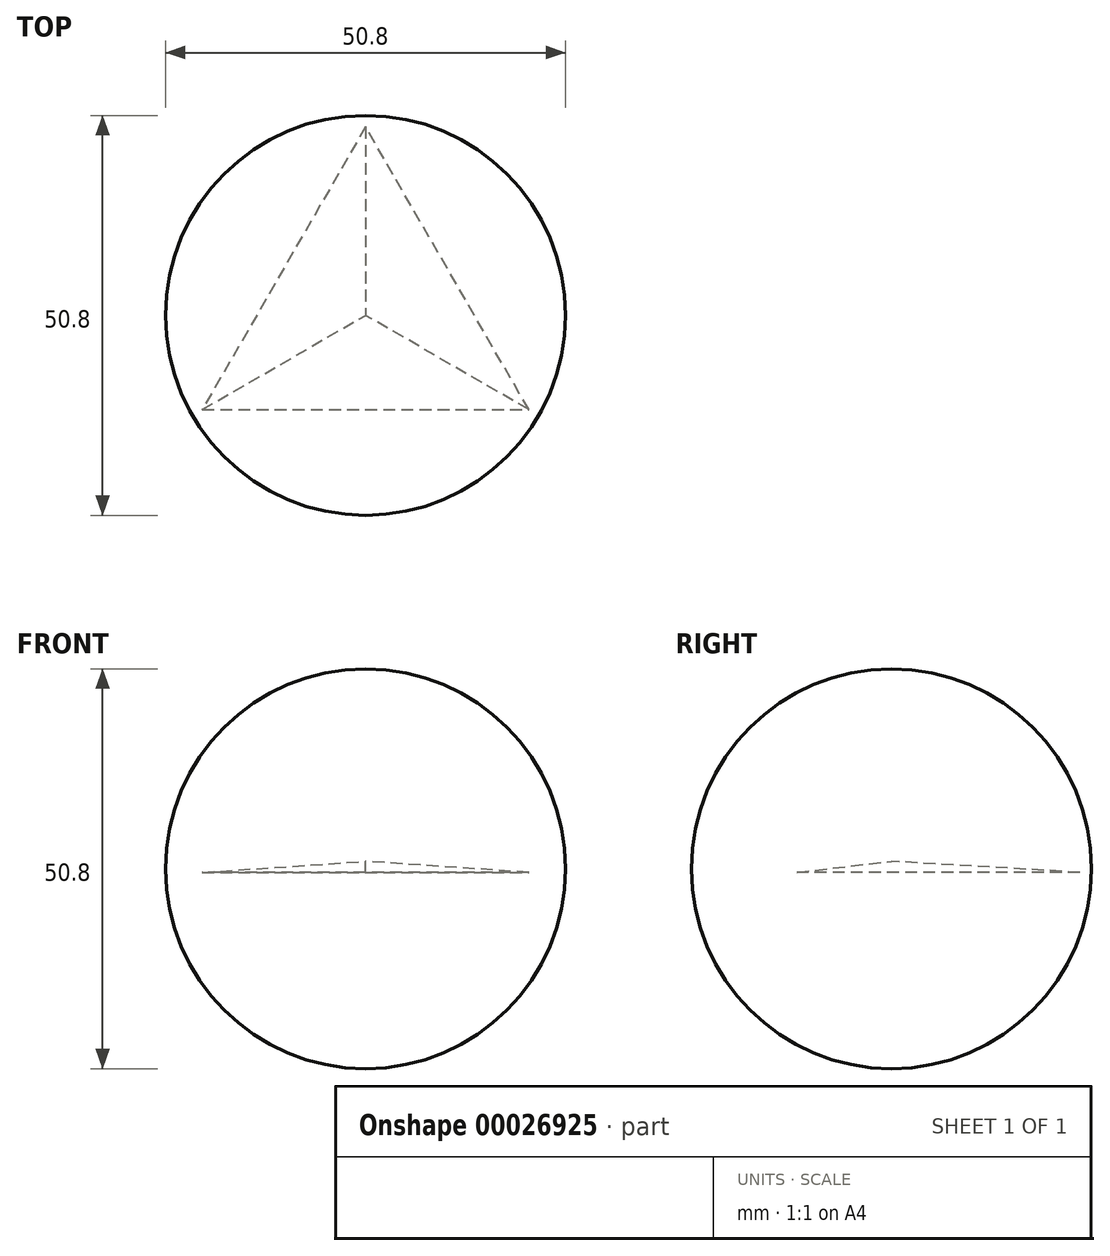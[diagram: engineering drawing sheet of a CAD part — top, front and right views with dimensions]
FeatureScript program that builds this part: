
annotation { "Feature Type Name" : "Feature", "Feature Type Description" : "" }
export const myFeature = defineFeature(function(context is Context, id is Id, definition is map)
    precondition{}
    {
        {
            assignVariable(context, id + "F0", {"name" : "r", "anyValue" : 1});
        }
        {
            assignVariable(context, id + "F1", {"name" : "s", "anyValue" : sqrt(8 / 3) * getVariable(context, 'r')});
        }
        {
            assignVariable(context, id + "F2", {"name" : "h", "anyValue" : sqrt((getVariable(context, 's')) ^ 2 - (getVariable(context, 's') / 2) ^ 2)});
        }
        {
            var Q0;
            Q0=qCreatedBy(makeId("Top.planeOp"),FACE);
            var sketch = newSketch(context, id + "F3", { "sketchPlane" : qUnion([Q0])});
            skLineSegment(sketch, "E0", {"start": v(0, 0) * mm, "end": v(0, 25.4) * mm});
            skLineSegment(sketch, "E1", {"start": v(0, 0) * mm, "end": v(25.4, 0) * mm});
            skArc(sketch, "E2", {"start": v(25.4, 0) * mm, "mid": v(17.96, 17.96) * mm, "end": v(0, 25.4) * mm});
            skSolve(sketch);
        }
        {
            var Q0;
            Q0=makeQuery(id+"F3.imprint","IMPRINT",FACE,{"disambiguationData":[TD([[makeQuery(id+"F3.imprint","IMPRINT",EDGE,{"derivedFrom":sQuery(id+"F3.wireOp",EDGE,"E0")}),-1.0]])]});
            var Q1;
            Q1=sQuery(id+"F3.wireOp",EDGE,"E0");
            revolve(context, id + "F4", {"entities" : qUnion([Q0]), "axis" : qUnion([Q1]), "revolveType" : RevolveType.FULL});
        }
        {
            var Q0;
            Q0=makeQuery(id+"F4.opRevolve","SWEPT_BODY",BODY,{"disambiguationData":[OSD([sQuery(id+"F3.wireOp",EDGE,"E0"),sQuery(id+"F3.wireOp",EDGE,"E1"),sQuery(id+"F3.wireOp",EDGE,"E2")])]});
            var Q1;
            Q1=qCreatedBy(makeId("Front.planeOp"),FACE);
            mirror(context, id + "F5", {"operationType" : NewBodyOperationType.ADD, "entities" : qUnion([Q0]), "mirrorPlane" : qUnion([Q1])});
        }
        {
            var Q0;
            Q0=qCreatedBy(makeId("Top.planeOp"),FACE);
            cPlane(context, id + "F6", {"entities" : qUnion([Q0]), "cplaneType" : CPlaneType.OFFSET, "offset" : ((getVariable(context, 's') / 2) * tan(30 * degree)) * mm, "oppositeDirection" : true, "width" : 152.4 * mm, "height" : 152.4 * mm});
        }
        {
            var Q0;
            Q0=qCreatedBy(id+"F6.planeOp",FACE);
            var sketch = newSketch(context, id + "F7", { "sketchPlane" : qUnion([Q0])});
            skLineSegment(sketch, "E3", {"start": v(-20.74, -11.97) * mm, "end": v(20.74, -11.97) * mm});
            skLineSegment(sketch, "E4", {"start": v(20.74, -11.97) * mm, "end": v(0, 23.95) * mm});
            skLineSegment(sketch, "E5", {"start": v(0, 23.95) * mm, "end": v(-20.74, -11.97) * mm});
            skSolve(sketch);
        }
        {
            var Q0;
            Q0=qCreatedBy(makeId("Top.planeOp"),FACE);
            cPlane(context, id + "F8", {"entities" : qUnion([Q0]), "cplaneType" : CPlaneType.OFFSET, "offset" : (getVariable(context, 'h') - (getVariable(context, 's') / 2) * tan(30 * degree)) * mm, "width" : 152.4 * mm, "height" : 152.4 * mm});
        }
        {
            var Q0;
            Q0=qCreatedBy(id+"F8.planeOp",FACE);
            var sketch = newSketch(context, id + "F9", { "sketchPlane" : qUnion([Q0])});
            skPoint(sketch, "E6", {"position": v(0, 0) * mm});
            skSolve(sketch);
        }
        {
            var Q0;
            Q0=makeQuery(id+"F7.imprint","IMPRINT",FACE,{"disambiguationData":[TD([[makeQuery(id+"F7.imprint","IMPRINT",EDGE,{"derivedFrom":sQuery(id+"F7.wireOp",EDGE,"E3")}),1.0]])]});
            var Q1;
            Q1=sQuery(id+"F9.wireOp",VERTEX,"E6");
            loft(context, id + "F10", {"sheetProfilesArray" : [{ "sheetProfileEntities" : qUnion([Q0]) }, { "sheetProfileEntities" : qUnion([Q1]) }]});
        }
    });
